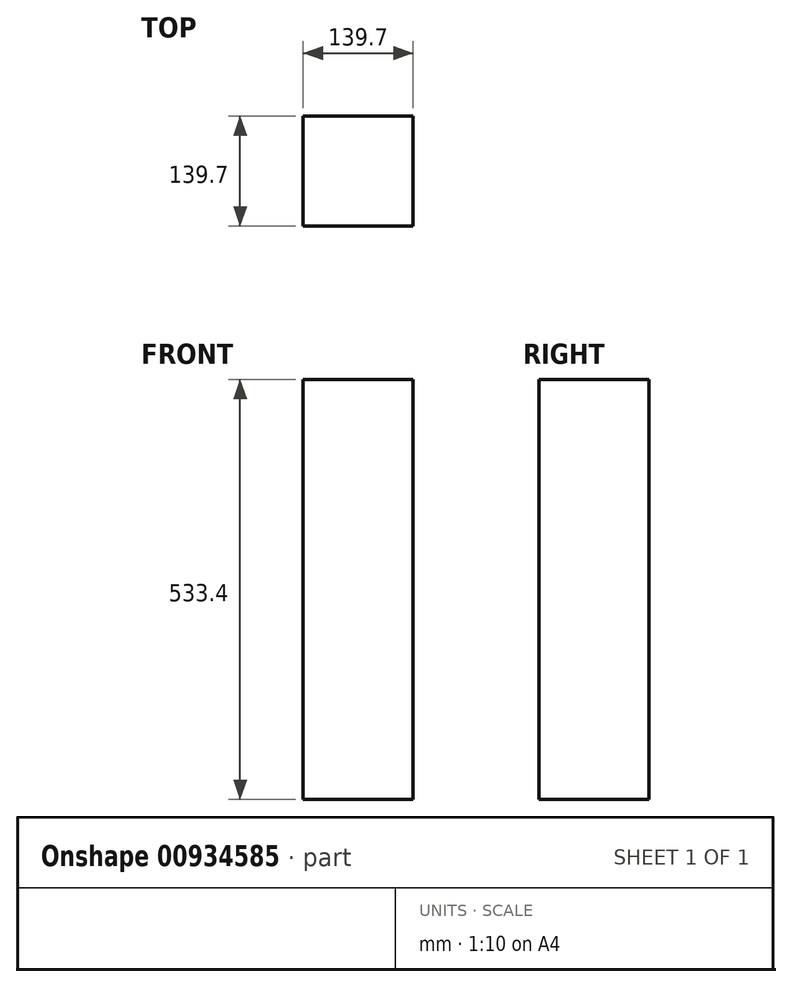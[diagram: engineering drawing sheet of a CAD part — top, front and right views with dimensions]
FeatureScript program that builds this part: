
annotation { "Feature Type Name" : "Feature", "Feature Type Description" : "" }
export const myFeature = defineFeature(function(context is Context, id is Id, definition is map)
    precondition{}
    {
        {
            var Q0;
            Q0=qCreatedBy(makeId("Top.planeOp"),FACE);
            var sketch = newSketch(context, id + "F0", { "sketchPlane" : qUnion([Q0])});
            skLineSegment(sketch, "E0.bottom", {"start": v(1232.28, -1185.42) * mm, "end": v(1371.98, -1185.42) * mm});
            skLineSegment(sketch, "E0.top", {"start": v(1232.28, -1325.12) * mm, "end": v(1371.98, -1325.12) * mm});
            skLineSegment(sketch, "E0.left", {"start": v(1232.28, -1185.42) * mm, "end": v(1232.28, -1325.12) * mm});
            skLineSegment(sketch, "E0.right", {"start": v(1371.98, -1185.42) * mm, "end": v(1371.98, -1325.12) * mm});
            skSolve(sketch);
        }
        {
            var Q0;
            Q0=makeQuery(id+"F0.imprint","IMPRINT",FACE,{"disambiguationData":[TD([[makeQuery(id+"F0.imprint","IMPRINT",EDGE,{"derivedFrom":sQuery(id+"F0.wireOp",EDGE,"E0.bottom")}),-1.0]])]});
            extrude(context, id + "F1", {"entities" : qUnion([Q0]), "depth" : 533.4 * mm, "offsetDistance" : 25.4 * mm});
        }
    });
